# Revit family: P191568KX-109c_KSEG700E
name_source: partatom
category: Specialty Equipment
units: mm (PartAtom-declared; Revit-internal decimal feet)

## family parameters
Always vertical = Yes
Cut with Voids When Loaded = No
Enable Cutting in Views = No
Maintain Annotation Orientation = No
Part Type = Normal
Room Calculation Point = No
Round Connector Dimension = Use Diameter
Shared = No
Work Plane-Based = No

## types (2) — shared parameters
Amps = 0 A
Clearance Material = ARCAT - Clearance
Cooktop Material = ARCAT - Glass - Tempered - Black
Default Elevation = 0"
Depth = 28 7/8"
Description = 30-Inch 5-Element Electric Slide-In Convection Range
Dimension Guide = http://access.whirlpool.com Guide&sku=KSEG700EBS&language=EN
Family Name = COOKING
Feature 1 = Even-Heat™ True Convection
Feature 2 = Steam Rack
Feature 3 = 6.4 cu ft Capacity
Glass Material = ARCAT - Glass - Tempered - Black
Handle Material = ARCAT - Metal - Steel - Gray
Height = 36"
Installation-Fabrication = http://access.whirlpool.com Instruction&sku=KSEG700EBS&language=EN
Knob Material = ARCAT - Metal - Steel - Gray
Leg Material = ARCAT - Metal - Steel - Stainless
Manufacturer = KitchenAid
Voltage = 0 V
Width = 29 7/8"

## per-type parameters (varying)
| type | Body Material | Door Material |
| KSEG700ESS | ARCAT - Metal - Steel - Stainless | ARCAT - Metal - Steel - Stainless |
| KSEG700EBS | ARCAT - Metal - Steel - Black Stainless | ARCAT - Metal - Steel - Black Stainless |

note: column(s) folded — value = type name in every type: Model

## geometry (parser evidence)
native form markers: Sweep x4
no freeform markers — native parametric forms only
